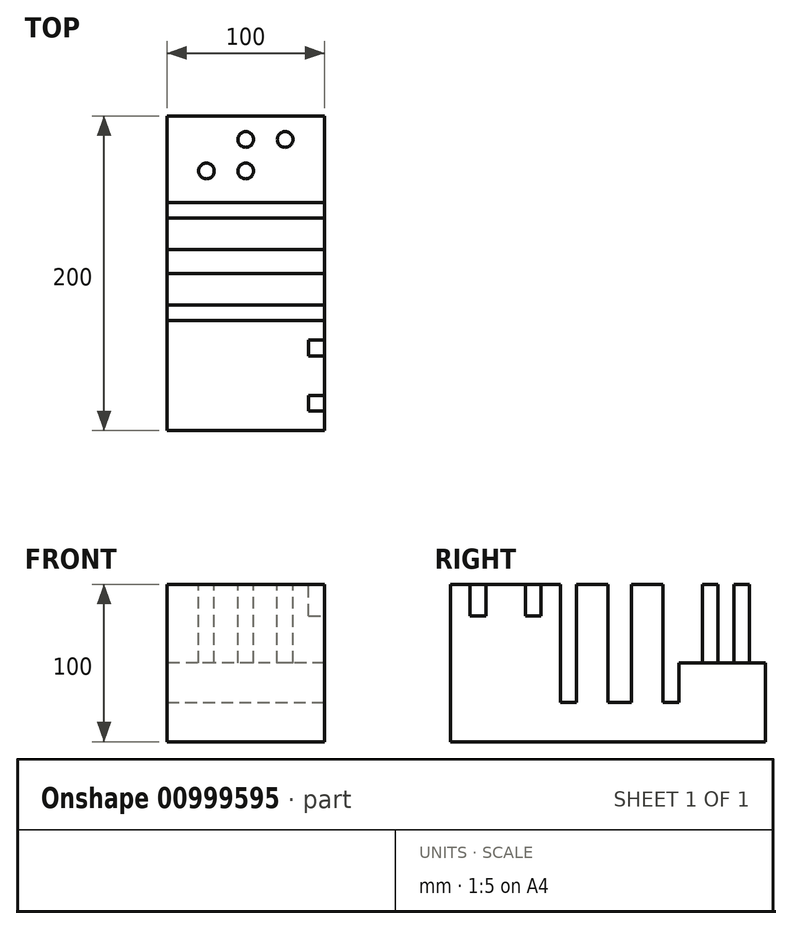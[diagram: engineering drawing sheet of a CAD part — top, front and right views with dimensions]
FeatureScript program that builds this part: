
annotation { "Feature Type Name" : "Feature", "Feature Type Description" : "" }
export const myFeature = defineFeature(function(context is Context, id is Id, definition is map)
    precondition{}
    {
        {
            var Q0;
            Q0=qCreatedBy(makeId("Top.planeOp"),FACE);
            var sketch = newSketch(context, id + "F0", { "sketchPlane" : qUnion([Q0])});
            skLineSegment(sketch, "E0.bottom", {"start": v(50, 100) * mm, "end": v(-50, 100) * mm});
            skLineSegment(sketch, "E0.top", {"start": v(50, -100) * mm, "end": v(-50, -100) * mm});
            skLineSegment(sketch, "E0.left", {"start": v(50, 100) * mm, "end": v(50, -100) * mm});
            skLineSegment(sketch, "E0.right", {"start": v(-50, 100) * mm, "end": v(-50, -100) * mm});
            skPoint(sketch, "E0.middle", {"position": v(0, 0) * mm});
            skLineSegment(sketch, "E1", {"start": v(-50, -35) * mm, "end": v(50, -35) * mm});
            skLineSegment(sketch, "E2.bottom", {"start": v(50, -45) * mm, "end": v(38.48, -45) * mm});
            skLineSegment(sketch, "E2.top", {"start": v(50, -55) * mm, "end": v(38.48, -55) * mm});
            skLineSegment(sketch, "E2.left", {"start": v(50, -45) * mm, "end": v(50, -55) * mm});
            skLineSegment(sketch, "E2.right", {"start": v(38.48, -45) * mm, "end": v(38.48, -55) * mm});
            skLineSegment(sketch, "E3.bottom", {"start": v(50, -80) * mm, "end": v(38.48, -80) * mm});
            skLineSegment(sketch, "E3.top", {"start": v(50, -90) * mm, "end": v(38.48, -90) * mm});
            skLineSegment(sketch, "E3.left", {"start": v(50, -80) * mm, "end": v(50, -90) * mm});
            skLineSegment(sketch, "E3.right", {"start": v(38.48, -80) * mm, "end": v(38.48, -90) * mm});
            skSolve(sketch);
        }
        {
            var Q0;
            Q0=makeQuery(id+"F0.imprint","IMPRINT",FACE,{"disambiguationData":[TD([[makeQuery(id+"F0.imprint","IMPRINT",EDGE,{"derivedFrom":sQuery(id+"F0.wireOp",EDGE,"E0.bottom")}),1.0]])]});
            extrude(context, id + "F1", {"entities" : qUnion([Q0]), "depth" : 100 * mm, "offsetDistance" : 25 * mm});
        }
        {
            var Q0;
            {var subQ0=sQuery(id+"F0.wireOp",EDGE,"E0.top");Q0=makeQuery(id+"F0.imprint","IMPRINT",FACE,{"disambiguationData":[TD([[makeQuery(id+"F0.imprint","IMPRINT",EDGE,{"derivedFrom":subQ0}),-1.0]])]});}
            var Q1;
            {var subQ0=sQuery(id+"F0.wireOp",EDGE,"E2.bottom");Q1=makeQuery(id+"F0.imprint","IMPRINT",FACE,{"disambiguationData":[TD([[makeQuery(id+"F0.imprint","IMPRINT",EDGE,{"derivedFrom":subQ0}),1.0]])]});}
            var Q2;
            {var subQ2=sQuery(id+"F0.wireOp",EDGE,"E3.bottom");Q2=makeQuery(id+"F0.imprint","IMPRINT",FACE,{"disambiguationData":[TD([[makeQuery(id+"F0.imprint","IMPRINT",EDGE,{"derivedFrom":subQ2}),1.0]])]});}
            extrude(context, id + "F2", {"entities" : qUnion([Q0, Q1, Q2]), "operationType" : NewBodyOperationType.ADD, "depth" : 100 * mm, "offsetDistance" : 25 * mm});
        }
        {
            var Q0;
            {var subQ0=sQuery(id+"F0.wireOp",EDGE,"E1");var subQ1=sQuery(id+"F0.wireOp",EDGE,"E0.right");var subQ2=sQuery(id+"F0.wireOp",EDGE,"E0.left");Q0=makeQuery(id+"F2.boolean.opBoolean","MERGE",FACE,{"derivedFrom":[makeQuery(id+"F1.opExtrude","CAP_FACE",FACE,{"disambiguationData":[OSD([sQuery(id+"F0.wireOp",EDGE,"E0.bottom"),subQ2,subQ1,subQ0])],"isStart":false}),makeQuery(id+"F2.opExtrude","CAP_FACE",FACE,{"disambiguationData":[OSD([sQuery(id+"F0.wireOp",EDGE,"E0.top"),subQ2,subQ1,subQ0])],"isStart":false})]});}
            var sketch = newSketch(context, id + "F3", { "sketchPlane" : qUnion([Q0])});
            skLineSegment(sketch, "E4", {"start": v(-50, 85) * mm, "end": v(50, 85) * mm});
            skLineSegment(sketch, "E5", {"start": v(50, 85) * mm, "end": v(50, 65) * mm});
            skLineSegment(sketch, "E6", {"start": v(50, 65) * mm, "end": v(-50, 65) * mm});
            skLineSegment(sketch, "E7", {"start": v(-50, 65) * mm, "end": v(-50, 85) * mm});
            skCircle(sketch, "E8", {"center": v(-25, 85) * mm, "radius": 5 * mm});
            skCircle(sketch, "E9", {"center": v(25, 85) * mm, "radius": 5 * mm});
            skCircle(sketch, "E10", {"center": v(-25, 65) * mm, "radius": 5 * mm});
            skCircle(sketch, "E11", {"center": v(25, 65) * mm, "radius": 5 * mm});
            skCircle(sketch, "E12", {"center": v(0, 85) * mm, "radius": 5 * mm});
            skCircle(sketch, "E13", {"center": v(0, 65) * mm, "radius": 5 * mm});
            skLineSegment(sketch, "E14.bottom", {"start": v(-50, 35) * mm, "end": v(50, 35) * mm});
            skLineSegment(sketch, "E14.top", {"start": v(-50, 45) * mm, "end": v(50, 45) * mm});
            skLineSegment(sketch, "E14.left", {"start": v(-50, 45) * mm, "end": v(-50, 35) * mm});
            skLineSegment(sketch, "E14.right", {"start": v(50, 45) * mm, "end": v(50, 35) * mm});
            skLineSegment(sketch, "E15.bottom", {"start": v(-50, 15) * mm, "end": v(50, 15) * mm});
            skLineSegment(sketch, "E15.top", {"start": v(-50, 0) * mm, "end": v(50, 0) * mm});
            skLineSegment(sketch, "E15.left", {"start": v(-50, 15) * mm, "end": v(-50, 0) * mm});
            skLineSegment(sketch, "E15.right", {"start": v(50, 15) * mm, "end": v(50, 0) * mm});
            skLineSegment(sketch, "E16.bottom", {"start": v(-50, -30) * mm, "end": v(50, -30) * mm});
            skLineSegment(sketch, "E16.top", {"start": v(-50, -20) * mm, "end": v(50, -20) * mm});
            skLineSegment(sketch, "E16.left", {"start": v(-50, -20) * mm, "end": v(-50, -30) * mm});
            skLineSegment(sketch, "E16.right", {"start": v(50, -20) * mm, "end": v(50, -30) * mm});
            skLineSegment(sketch, "E17.top", {"start": v(-50, -100) * mm, "end": v(50, -100) * mm});
            skLineSegment(sketch, "E17.left", {"start": v(-50, -30) * mm, "end": v(-50, -100) * mm});
            skLineSegment(sketch, "E17.right", {"start": v(50, -30) * mm, "end": v(50, -100) * mm});
            skSolve(sketch);
        }
        {
            var Q0;
            {var subQ0=sQuery(id+"F0.wireOp",EDGE,"E0.left");Q0=makeQuery(id+"F2.boolean.opBoolean","MERGE",FACE,{"derivedFrom":[makeQuery(id+"F1.opExtrude","SWEPT_FACE",FACE,{"disambiguationData":[OSD([subQ0])]}),makeQuery(id+"F2.opExtrude","SWEPT_FACE",FACE,{"disambiguationData":[OSD([subQ0])]})]});}
            var sketch = newSketch(context, id + "F4", { "sketchPlane" : qUnion([Q0])});
            skLineSegment(sketch, "E18.bottom", {"start": v(-30, 100) * mm, "end": v(-20, 100) * mm});
            skLineSegment(sketch, "E18.top", {"start": v(-30, 0) * mm, "end": v(-20, 0) * mm});
            skLineSegment(sketch, "E18.right", {"start": v(-20, 100) * mm, "end": v(-20, 0) * mm});
            skLineSegment(sketch, "E19.bottom", {"start": v(0, 100) * mm, "end": v(15, 100) * mm});
            skLineSegment(sketch, "E19.top", {"start": v(0, 0) * mm, "end": v(15, 0) * mm});
            skLineSegment(sketch, "E19.left", {"start": v(0, 100) * mm, "end": v(0, 0) * mm});
            skLineSegment(sketch, "E19.right", {"start": v(15, 100) * mm, "end": v(15, 0) * mm});
            skLineSegment(sketch, "E20.bottom", {"start": v(35.17, 100) * mm, "end": v(45.17, 100) * mm});
            skLineSegment(sketch, "E20.top", {"start": v(35.17, 0) * mm, "end": v(45.17, 0) * mm});
            skLineSegment(sketch, "E20.left", {"start": v(35.17, 100) * mm, "end": v(35.17, 0) * mm});
            skLineSegment(sketch, "E20.right", {"start": v(45.17, 100) * mm, "end": v(45.17, 0) * mm});
            skLineSegment(sketch, "E21", {"start": v(-30, 100) * mm, "end": v(-30, 0) * mm});
            skLineSegment(sketch, "E22.bottom", {"start": v(-87.5, 100) * mm, "end": v(-77.5, 100) * mm});
            skLineSegment(sketch, "E22.top", {"start": v(-87.5, 80) * mm, "end": v(-77.5, 80) * mm});
            skLineSegment(sketch, "E22.left", {"start": v(-87.5, 100) * mm, "end": v(-87.5, 80) * mm});
            skLineSegment(sketch, "E22.right", {"start": v(-77.5, 100) * mm, "end": v(-77.5, 80) * mm});
            skLineSegment(sketch, "E23.bottom", {"start": v(-52.5, 80) * mm, "end": v(-42.5, 80) * mm});
            skLineSegment(sketch, "E23.top", {"start": v(-52.5, 100) * mm, "end": v(-42.5, 100) * mm});
            skLineSegment(sketch, "E23.left", {"start": v(-52.5, 80) * mm, "end": v(-52.5, 100) * mm});
            skLineSegment(sketch, "E23.right", {"start": v(-42.5, 80) * mm, "end": v(-42.5, 100) * mm});
            skSolve(sketch);
        }
        {
            var Q0;
            Q0=makeQuery(id+"F3.imprint","IMPRINT",FACE,{"disambiguationData":[TD([[makeQuery(id+"F3.imprint","IMPRINT",EDGE,{"derivedFrom":sQuery(id+"F3.wireOp",EDGE,"E16.top")}),-1.0]])]});
            var Q1;
            Q1=makeQuery(id+"F3.imprint","IMPRINT",FACE,{"disambiguationData":[TD([[makeQuery(id+"F3.imprint","IMPRINT",EDGE,{"derivedFrom":sQuery(id+"F3.wireOp",EDGE,"E15.bottom")}),-1.0]])]});
            var Q2;
            Q2=makeQuery(id+"F3.imprint","IMPRINT",FACE,{"disambiguationData":[TD([[makeQuery(id+"F3.imprint","IMPRINT",EDGE,{"derivedFrom":sQuery(id+"F3.wireOp",EDGE,"E14.bottom")}),1.0]])]});
            extrude(context, id + "F5", {"entities" : qUnion([Q0, Q1, Q2]), "operationType" : NewBodyOperationType.REMOVE, "oppositeDirection" : true, "depth" : 75 * mm, "offsetDistance" : 25 * mm});
        }
        {
            var Q0;
            {var subQ0=sQuery(id+"F3.wireOp",EDGE,"E11");var subQ1=sQuery(id+"F3.wireOp",EDGE,"E6");var subQ2=makeQuery(id+"F3.imprint","INTERSECT",VERTEX,{"disambiguationData":[OD(0.0)],"derivedFrom":[subQ1,subQ0]});Q0=makeQuery(id+"F3.imprint","IMPRINT",FACE,{"disambiguationData":[TD([[makeQuery(id+"F3.imprint","IMPRINT",EDGE,{"disambiguationData":[TD([[subQ2,-1.0]])],"derivedFrom":subQ1}),1.0]])]});}
            var Q1;
            {var subQ0=sQuery(id+"F3.wireOp",EDGE,"E11");var subQ1=sQuery(id+"F3.wireOp",EDGE,"E6");var subQ2=makeQuery(id+"F3.imprint","INTERSECT",VERTEX,{"disambiguationData":[OD(0.0)],"derivedFrom":[subQ1,subQ0]});Q1=makeQuery(id+"F3.imprint","IMPRINT",FACE,{"disambiguationData":[TD([[makeQuery(id+"F3.imprint","IMPRINT",EDGE,{"disambiguationData":[TD([[subQ2,-1.0]])],"derivedFrom":subQ1}),-1.0]])]});}
            var Q2;
            {var subQ0=sQuery(id+"F3.wireOp",EDGE,"E13");var subQ1=sQuery(id+"F3.wireOp",EDGE,"E6");var subQ2=makeQuery(id+"F3.imprint","INTERSECT",VERTEX,{"disambiguationData":[OD(0.0)],"derivedFrom":[subQ1,subQ0]});Q2=makeQuery(id+"F3.imprint","IMPRINT",FACE,{"disambiguationData":[TD([[makeQuery(id+"F3.imprint","IMPRINT",EDGE,{"disambiguationData":[TD([[subQ2,-1.0]])],"derivedFrom":subQ1}),1.0]])]});}
            var Q3;
            {var subQ0=sQuery(id+"F3.wireOp",EDGE,"E13");var subQ1=sQuery(id+"F3.wireOp",EDGE,"E6");var subQ2=makeQuery(id+"F3.imprint","INTERSECT",VERTEX,{"disambiguationData":[OD(0.0)],"derivedFrom":[subQ1,subQ0]});Q3=makeQuery(id+"F3.imprint","IMPRINT",FACE,{"disambiguationData":[TD([[makeQuery(id+"F3.imprint","IMPRINT",EDGE,{"disambiguationData":[TD([[subQ2,-1.0]])],"derivedFrom":subQ1}),-1.0]])]});}
            var Q4;
            {var subQ0=sQuery(id+"F3.wireOp",EDGE,"E10");var subQ1=sQuery(id+"F3.wireOp",EDGE,"E6");var subQ2=makeQuery(id+"F3.imprint","INTERSECT",VERTEX,{"disambiguationData":[OD(0.0)],"derivedFrom":[subQ1,subQ0]});Q4=makeQuery(id+"F3.imprint","IMPRINT",FACE,{"disambiguationData":[TD([[makeQuery(id+"F3.imprint","IMPRINT",EDGE,{"disambiguationData":[TD([[subQ2,-1.0]])],"derivedFrom":subQ1}),1.0]])]});}
            var Q5;
            {var subQ0=sQuery(id+"F3.wireOp",EDGE,"E10");var subQ1=sQuery(id+"F3.wireOp",EDGE,"E6");var subQ2=makeQuery(id+"F3.imprint","INTERSECT",VERTEX,{"disambiguationData":[OD(0.0)],"derivedFrom":[subQ1,subQ0]});Q5=makeQuery(id+"F3.imprint","IMPRINT",FACE,{"disambiguationData":[TD([[makeQuery(id+"F3.imprint","IMPRINT",EDGE,{"disambiguationData":[TD([[subQ2,-1.0]])],"derivedFrom":subQ1}),-1.0]])]});}
            var Q6;
            {var subQ0=sQuery(id+"F3.wireOp",EDGE,"E8");var subQ1=sQuery(id+"F3.wireOp",EDGE,"E4");var subQ2=makeQuery(id+"F3.imprint","INTERSECT",VERTEX,{"disambiguationData":[OD(0.0)],"derivedFrom":[subQ1,subQ0]});Q6=makeQuery(id+"F3.imprint","IMPRINT",FACE,{"disambiguationData":[TD([[makeQuery(id+"F3.imprint","IMPRINT",EDGE,{"disambiguationData":[TD([[subQ2,-1.0]])],"derivedFrom":subQ1}),-1.0]])]});}
            var Q7;
            {var subQ0=sQuery(id+"F3.wireOp",EDGE,"E8");var subQ1=sQuery(id+"F3.wireOp",EDGE,"E4");var subQ2=makeQuery(id+"F3.imprint","INTERSECT",VERTEX,{"disambiguationData":[OD(0.0)],"derivedFrom":[subQ1,subQ0]});Q7=makeQuery(id+"F3.imprint","IMPRINT",FACE,{"disambiguationData":[TD([[makeQuery(id+"F3.imprint","IMPRINT",EDGE,{"disambiguationData":[TD([[subQ2,-1.0]])],"derivedFrom":subQ1}),1.0]])]});}
            var Q8;
            {var subQ0=sQuery(id+"F3.wireOp",EDGE,"E12");var subQ1=sQuery(id+"F3.wireOp",EDGE,"E4");var subQ2=makeQuery(id+"F3.imprint","INTERSECT",VERTEX,{"disambiguationData":[OD(0.0)],"derivedFrom":[subQ1,subQ0]});Q8=makeQuery(id+"F3.imprint","IMPRINT",FACE,{"disambiguationData":[TD([[makeQuery(id+"F3.imprint","IMPRINT",EDGE,{"disambiguationData":[TD([[subQ2,-1.0]])],"derivedFrom":subQ1}),1.0]])]});}
            var Q9;
            {var subQ0=sQuery(id+"F3.wireOp",EDGE,"E12");var subQ1=sQuery(id+"F3.wireOp",EDGE,"E4");var subQ2=makeQuery(id+"F3.imprint","INTERSECT",VERTEX,{"disambiguationData":[OD(0.0)],"derivedFrom":[subQ1,subQ0]});Q9=makeQuery(id+"F3.imprint","IMPRINT",FACE,{"disambiguationData":[TD([[makeQuery(id+"F3.imprint","IMPRINT",EDGE,{"disambiguationData":[TD([[subQ2,-1.0]])],"derivedFrom":subQ1}),-1.0]])]});}
            var Q10;
            {var subQ0=sQuery(id+"F3.wireOp",EDGE,"E9");var subQ1=sQuery(id+"F3.wireOp",EDGE,"E4");var subQ2=makeQuery(id+"F3.imprint","INTERSECT",VERTEX,{"disambiguationData":[OD(0.0)],"derivedFrom":[subQ1,subQ0]});Q10=makeQuery(id+"F3.imprint","IMPRINT",FACE,{"disambiguationData":[TD([[makeQuery(id+"F3.imprint","IMPRINT",EDGE,{"disambiguationData":[TD([[subQ2,-1.0]])],"derivedFrom":subQ1}),-1.0]])]});}
            var Q11;
            {var subQ0=sQuery(id+"F3.wireOp",EDGE,"E9");var subQ1=sQuery(id+"F3.wireOp",EDGE,"E4");var subQ2=makeQuery(id+"F3.imprint","INTERSECT",VERTEX,{"disambiguationData":[OD(0.0)],"derivedFrom":[subQ1,subQ0]});Q11=makeQuery(id+"F3.imprint","IMPRINT",FACE,{"disambiguationData":[TD([[makeQuery(id+"F3.imprint","IMPRINT",EDGE,{"disambiguationData":[TD([[subQ2,-1.0]])],"derivedFrom":subQ1}),1.0]])]});}
            extrude(context, id + "F6", {"entities" : qUnion([Q0, Q1, Q2, Q3, Q4, Q5, Q6, Q7, Q8, Q9, Q10, Q11]), "operationType" : NewBodyOperationType.REMOVE, "oppositeDirection" : true, "depth" : 50 * mm, "offsetDistance" : 25 * mm});
        }
        {
            var Q0;
            Q0=makeQuery(id+"F4.imprint","IMPRINT",FACE,{"disambiguationData":[TD([[makeQuery(id+"F4.imprint","IMPRINT",EDGE,{"derivedFrom":sQuery(id+"F4.wireOp",EDGE,"E22.bottom")}),1.0]])]});
            var Q1;
            Q1=makeQuery(id+"F4.imprint","IMPRINT",FACE,{"disambiguationData":[TD([[makeQuery(id+"F4.imprint","IMPRINT",EDGE,{"derivedFrom":sQuery(id+"F4.wireOp",EDGE,"E23.bottom")}),1.0]])]});
            extrude(context, id + "F7", {"entities" : qUnion([Q0, Q1]), "operationType" : NewBodyOperationType.REMOVE, "oppositeDirection" : true, "depth" : 10 * mm, "offsetDistance" : 25 * mm});
        }
    });
